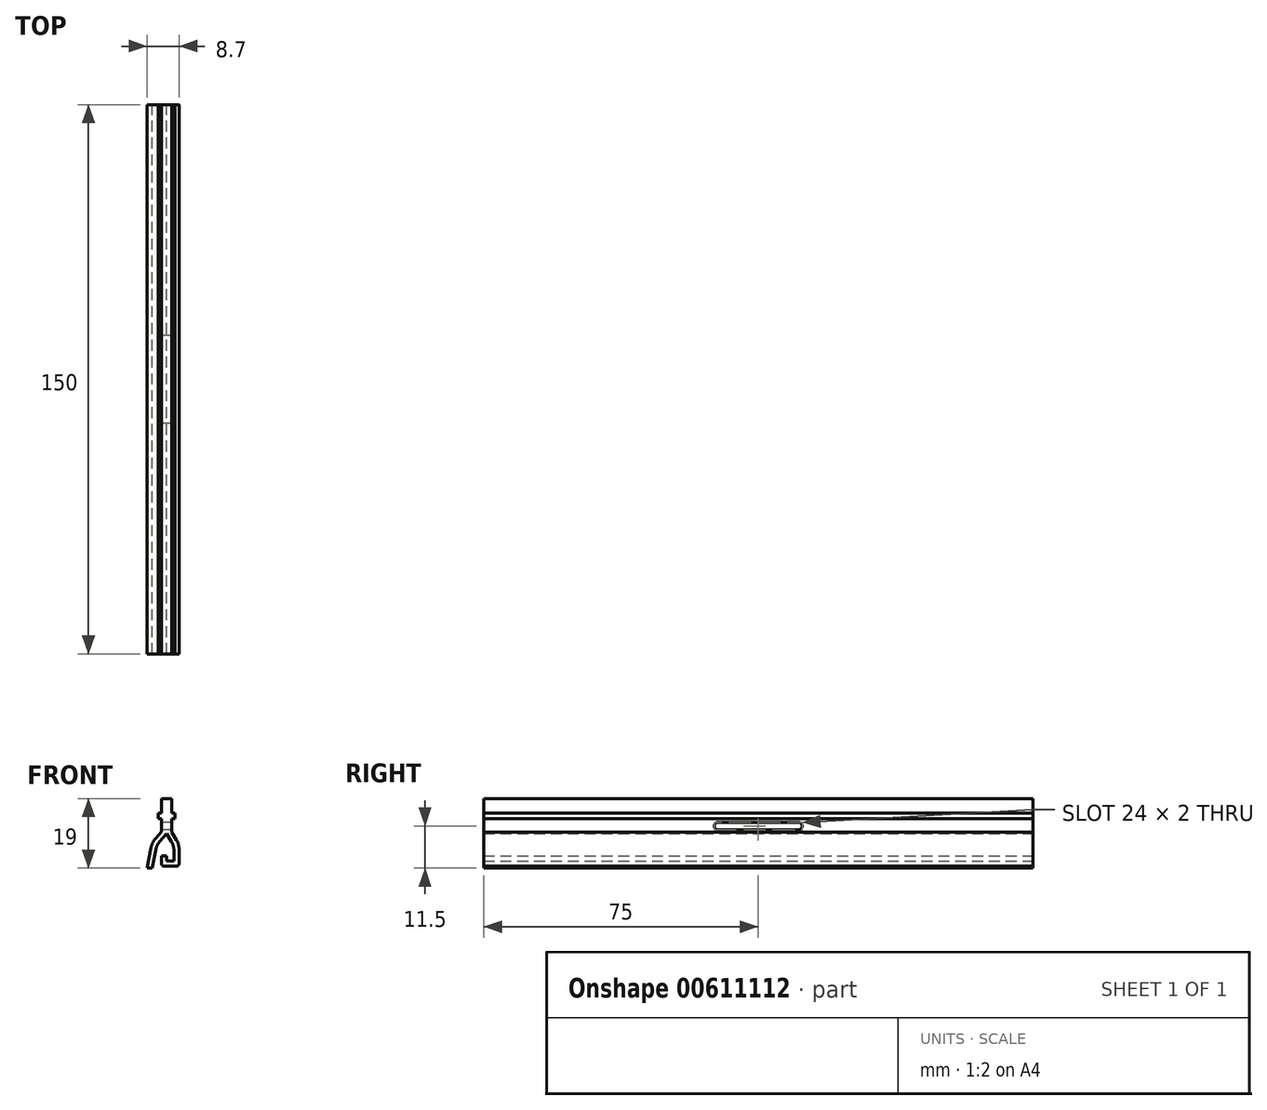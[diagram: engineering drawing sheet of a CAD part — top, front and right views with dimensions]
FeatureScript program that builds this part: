
annotation { "Feature Type Name" : "Feature", "Feature Type Description" : "" }
export const myFeature = defineFeature(function(context is Context, id is Id, definition is map)
    precondition{}
    {
        {
            var Q0;
            Q0=qCreatedBy(makeId("Front.planeOp"),FACE);
            var sketch = newSketch(context, id + "F0", { "sketchPlane" : qUnion([Q0])});
            skLineSegment(sketch, "E0", {"start": v(-1.4, 9) * mm, "end": v(-1.4, 5) * mm});
            skLineSegment(sketch, "E1", {"start": v(-1.4, 9) * mm, "end": v(1.4, 9) * mm});
            skLineSegment(sketch, "E2", {"start": v(1.4, 9) * mm, "end": v(1.4, 5) * mm});
            skPoint(sketch, "E3.orphan", {"position": v(1.4, 0) * mm});
            skLineSegment(sketch, "E4", {"start": v(1.4, -0.14) * mm, "end": v(2.7, -2.32) * mm});
            skLineSegment(sketch, "E5", {"start": v(3.4, -4.87) * mm, "end": v(3.4, -8.75) * mm});
            skLineSegment(sketch, "E6", {"start": v(2.65, -9.5) * mm, "end": v(-0.65, -9.5) * mm});
            skLineSegment(sketch, "E7", {"start": v(-1.4, -8.75) * mm, "end": v(-1.4, -6.7) * mm});
            skLineSegment(sketch, "E8.0", {"start": v(0, -0.52) * mm, "end": v(1.3, -2.7) * mm});
            skLineSegment(sketch, "E9.0", {"start": v(2, -5.26) * mm, "end": v(2, -8.1) * mm});
            skLineSegment(sketch, "E10.0", {"start": v(2, -8.1) * mm, "end": v(0, -8.1) * mm});
            skLineSegment(sketch, "E11.0", {"start": v(0, -8.1) * mm, "end": v(0, -6.7) * mm});
            skLineSegment(sketch, "E12", {"start": v(-1.4, -6.7) * mm, "end": v(0, -6.7) * mm});
            skLineSegment(sketch, "E13", {"start": v(-1.4, 0) * mm, "end": v(-2.93, -1.77) * mm});
            skLineSegment(sketch, "E14", {"start": v(-4.3, -4.6) * mm, "end": v(-5.3, -10) * mm});
            skPoint(sketch, "E15.visualSharp", {"position": v(-4, -3) * mm});
            skArc(sketch, "E15.filletArc", {"start": v(-2.93, -1.77) * mm, "mid": v(-3.8, -3.1) * mm, "end": v(-4.3, -4.6) * mm});
            skLineSegment(sketch, "E16.0", {"start": v(-2.9, -4.73) * mm, "end": v(-3.88, -10) * mm});
            skArc(sketch, "E17.0", {"start": v(-1.87, -2.69) * mm, "mid": v(-2.54, -3.7) * mm, "end": v(-2.92, -4.86) * mm});
            skLineSegment(sketch, "E18.0", {"start": v(0, -0.52) * mm, "end": v(-1.87, -2.69) * mm});
            skLineSegment(sketch, "E19", {"start": v(-5.3, -10) * mm, "end": v(-3.88, -10) * mm});
            skPoint(sketch, "E20.visualSharp", {"position": v(3.4, -3.5) * mm});
            skArc(sketch, "E20.filletArc", {"start": v(3.4, -4.87) * mm, "mid": v(3.22, -3.55) * mm, "end": v(2.7, -2.32) * mm});
            skPoint(sketch, "E21.visualSharp", {"position": v(2, -3.88) * mm});
            skArc(sketch, "E21.filletArc", {"start": v(2, -5.26) * mm, "mid": v(1.82, -3.93) * mm, "end": v(1.3, -2.7) * mm});
            skPoint(sketch, "E22.visualSharp", {"position": v(3.4, -9.5) * mm});
            skArc(sketch, "E22.filletArc", {"start": v(2.65, -9.5) * mm, "mid": v(3.18, -9.28) * mm, "end": v(3.4, -8.75) * mm});
            skPoint(sketch, "E23.visualSharp", {"position": v(-1.4, -9.5) * mm});
            skArc(sketch, "E23.filletArc", {"start": v(-1.4, -8.75) * mm, "mid": v(-1.18, -9.28) * mm, "end": v(-0.65, -9.5) * mm});
            skLineSegment(sketch, "E24.bottom", {"start": v(-2.3, 5) * mm, "end": v(-1.4, 5) * mm});
            skLineSegment(sketch, "E24.top", {"start": v(-2.3, 3.5) * mm, "end": v(-1.4, 3.5) * mm});
            skLineSegment(sketch, "E24.left", {"start": v(-2.3, 5) * mm, "end": v(-2.3, 3.5) * mm});
            skLineSegment(sketch, "E25.bottom", {"start": v(1.4, 5) * mm, "end": v(2.3, 5) * mm});
            skLineSegment(sketch, "E25.top", {"start": v(1.4, 3.5) * mm, "end": v(2.3, 3.5) * mm});
            skLineSegment(sketch, "E25.right", {"start": v(2.3, 5) * mm, "end": v(2.3, 3.5) * mm});
            skLineSegment(sketch, "E26.trimOffspring", {"start": v(-1.4, 3.5) * mm, "end": v(-1.4, 0) * mm});
            skLineSegment(sketch, "E27.trimOffspring", {"start": v(1.4, 3.5) * mm, "end": v(1.4, -0.14) * mm});
            skSolve(sketch);
        }
        {
            var Q0;
            Q0 = qSketchRegion(id + "F0", true);
            extrude(context, id + "F1", {"entities" : qUnion([Q0]), "endBound" : BoundingType.SYMMETRIC, "depth" : 150 * mm, "offsetDistance" : 25 * mm});
        }
        {
            var Q0;
            Q0=qCreatedBy(makeId("Right.planeOp"),FACE);
            var sketch = newSketch(context, id + "F2", { "sketchPlane" : qUnion([Q0])});
            skLineSegment(sketch, "E28.bottom", {"start": v(11, 2.5) * mm, "end": v(-11, 2.5) * mm});
            skLineSegment(sketch, "E28.top", {"start": v(11, 0.5) * mm, "end": v(-11, 0.5) * mm});
            skLineSegment(sketch, "E28.left", {"start": v(12, 1.5) * mm, "end": v(12, 1.5) * mm});
            skLineSegment(sketch, "E28.right", {"start": v(-12, 1.5) * mm, "end": v(-12, 1.5) * mm});
            skPoint(sketch, "E29.visualSharp", {"position": v(12, 0.5) * mm});
            skArc(sketch, "E29.filletArc", {"start": v(11, 0.5) * mm, "mid": v(11.7, 0.8) * mm, "end": v(12, 1.5) * mm});
            skPoint(sketch, "E30.visualSharp", {"position": v(12, 2.5) * mm});
            skArc(sketch, "E30.filletArc", {"start": v(12, 1.5) * mm, "mid": v(11.7, 2.2) * mm, "end": v(11, 2.5) * mm});
            skPoint(sketch, "E31.visualSharp", {"position": v(-12, 2.5) * mm});
            skArc(sketch, "E31.filletArc", {"start": v(-11, 2.5) * mm, "mid": v(-11.7, 2.2) * mm, "end": v(-12, 1.5) * mm});
            skPoint(sketch, "E32.visualSharp", {"position": v(-12, 0.5) * mm});
            skArc(sketch, "E32.filletArc", {"start": v(-12, 1.5) * mm, "mid": v(-11.7, 0.8) * mm, "end": v(-11, 0.5) * mm});
            skSolve(sketch);
        }
        {
            var Q0;
            Q0 = qSketchRegion(id + "F2", true);
            extrude(context, id + "F3", {"entities" : qUnion([Q0]), "operationType" : NewBodyOperationType.REMOVE, "endBound" : BoundingType.SYMMETRIC, "depth" : 25 * mm, "offsetDistance" : 25 * mm});
        }
    });
